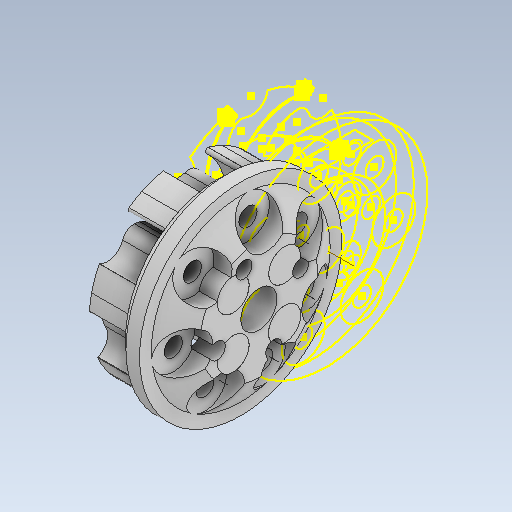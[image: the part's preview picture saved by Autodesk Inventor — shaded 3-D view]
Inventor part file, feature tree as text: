
AUTODESK INVENTOR PART (.ipt)
format: ipt  version: 2020 (Build 240168000, 168)  size: 627,200 bytes
history: native  units: in
note: dims shown in document units (in); Inventor stores cm internally (conversion verified against a paired STEP export)
features: sketch x16, other x3, plane x2, mirror x1
ambient origin geometry x8: Origin, YZ Plane, XZ Plane, XY Plane, X Axis, Y Axis, Z Axis, Center Point
bodies: Solid1 (feature_tree)
feature tree (22):
  mirror  "MirrorGoodAdap.ipt"
  other  "Solid1::MirrorGoodAdap.ipt"
  other  "TaggingFeature1"
  sketch  "Sketch1"  dims[d0=0.3937in]
  sketch  "Sketch3"
  sketch  "Sketch4"
  sketch  "Sketch5"
  sketch  "Sketch6"
  sketch  "Sketch7"
  sketch  "Sketch8"
  sketch  "Sketch9"
  sketch  "Sketch10"
  sketch  "Sketch11"
  sketch  "Sketch12"
  sketch  "Sketch14"
  sketch  "Sketch16"
  sketch  "Sketch17"
  sketch  "Sketch18"
  sketch  "Sketch19"
  plane  "Work Plane1"
  plane  "Work Plane2"
  other  "Work Axis1"
